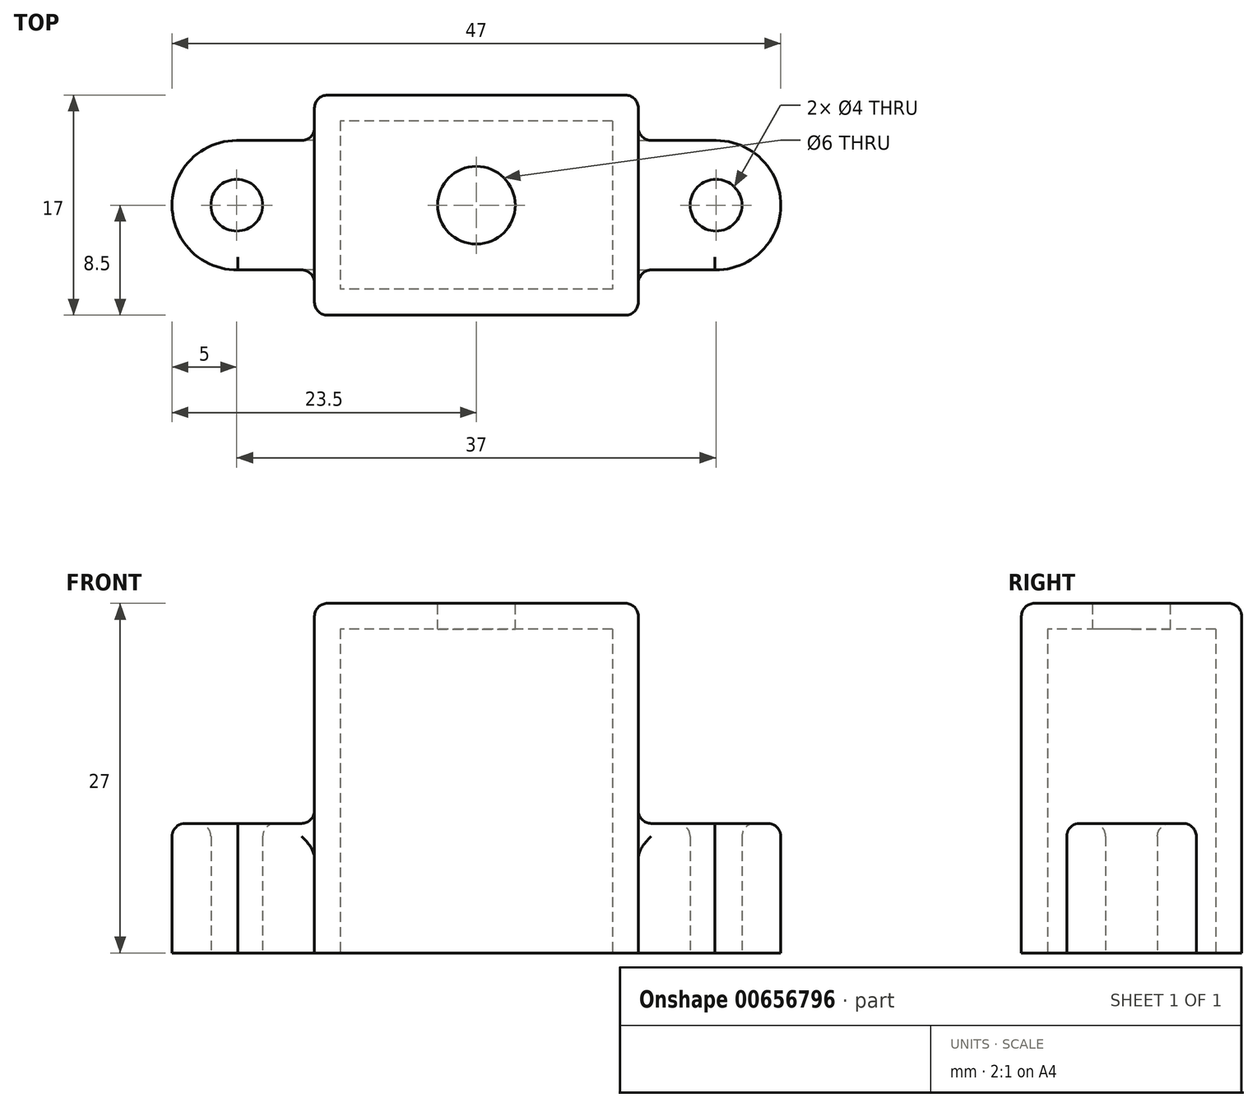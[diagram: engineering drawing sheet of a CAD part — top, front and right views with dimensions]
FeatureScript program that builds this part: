
annotation { "Feature Type Name" : "Feature", "Feature Type Description" : "" }
export const myFeature = defineFeature(function(context is Context, id is Id, definition is map)
    precondition{}
    {
        {
            var Q0;
            Q0=qCreatedBy(makeId("Top.planeOp"),FACE);
            var sketch = newSketch(context, id + "F0", { "sketchPlane" : qUnion([Q0])});
            skPoint(sketch, "E0.middle", {"position": v(0, 0) * mm});
            skLineSegment(sketch, "E1.bottom", {"start": v(12.5, -8.5) * mm, "end": v(-12.5, -8.5) * mm});
            skLineSegment(sketch, "E1.top", {"start": v(12.5, 8.5) * mm, "end": v(-12.5, 8.5) * mm});
            skLineSegment(sketch, "E1.left", {"start": v(12.5, -8.5) * mm, "end": v(12.5, 8.5) * mm});
            skLineSegment(sketch, "E1.right", {"start": v(-12.5, -8.5) * mm, "end": v(-12.5, 8.5) * mm});
            skSolve(sketch);
        }
        {
            var Q0;
            Q0 = qSketchRegion(id + "F0", true);
            extrude(context, id + "F1", {"entities" : qUnion([Q0]), "depth" : 27 * mm, "offsetDistance" : 25 * mm});
        }
        {
            var Q0;
            Q0=makeQuery(id+"F1.opExtrude","CAP_FACE",FACE,{"disambiguationData":[OSD([sQuery(id+"F0.wireOp",EDGE,"E1.bottom"),sQuery(id+"F0.wireOp",EDGE,"E1.top"),sQuery(id+"F0.wireOp",EDGE,"E1.left"),sQuery(id+"F0.wireOp",EDGE,"E1.right")])],"isStart":true});
            var sketch = newSketch(context, id + "F2", { "sketchPlane" : qUnion([Q0])});
            skLineSegment(sketch, "E2.bottom", {"start": v(10.5, -6.5) * mm, "end": v(-10.5, -6.5) * mm});
            skLineSegment(sketch, "E2.top", {"start": v(10.5, 6.5) * mm, "end": v(-10.5, 6.5) * mm});
            skLineSegment(sketch, "E2.left", {"start": v(10.5, -6.5) * mm, "end": v(10.5, 6.5) * mm});
            skLineSegment(sketch, "E2.right", {"start": v(-10.5, -6.5) * mm, "end": v(-10.5, 6.5) * mm});
            skPoint(sketch, "E2.middle", {"position": v(0, 0) * mm});
            skSolve(sketch);
        }
        {
            var Q0;
            Q0 = qSketchRegion(id + "F2", true);
            extrude(context, id + "F3", {"entities" : qUnion([Q0]), "operationType" : NewBodyOperationType.REMOVE, "oppositeDirection" : true, "depth" : 25 * mm, "offsetDistance" : 25 * mm});
        }
        {
            var Q0;
            Q0=qCreatedBy(makeId("Top.planeOp"),FACE);
            var sketch = newSketch(context, id + "F4", { "sketchPlane" : qUnion([Q0])});
            skArc(sketch, "E3", {"start": v(18.41, -5) * mm, "mid": v(23.5, -0.04) * mm, "end": v(18.5, 5) * mm});
            skLineSegment(sketch, "E4", {"start": v(18.5, 5) * mm, "end": v(12.5, 5) * mm});
            skLineSegment(sketch, "E5", {"start": v(12.5, 5) * mm, "end": v(12.5, -5) * mm});
            skLineSegment(sketch, "E6", {"start": v(12.5, -5) * mm, "end": v(18.59, -5) * mm});
            skCircle(sketch, "E7", {"center": v(18.5, 0) * mm, "radius": 2 * mm});
            skArc(sketch, "E8.MirrorCS", {"start": v(-18.41, -5) * mm, "mid": v(-23.5, -0.04) * mm, "end": v(-18.5, 5) * mm});
            skLineSegment(sketch, "E9.MirrorCS", {"start": v(-18.5, 5) * mm, "end": v(-12.5, 5) * mm});
            skLineSegment(sketch, "E10.MirrorCS", {"start": v(-12.5, -5) * mm, "end": v(-18.59, -5) * mm});
            skLineSegment(sketch, "E11.MirrorCS", {"start": v(-12.5, 5) * mm, "end": v(-12.5, -5) * mm});
            skCircle(sketch, "E12.MirrorC", {"center": v(-18.5, 0) * mm, "radius": 2 * mm});
            skSolve(sketch);
        }
        {
            var Q0;
            Q0 = qSketchRegion(id + "F4", true);
            extrude(context, id + "F5", {"entities" : qUnion([Q0]), "operationType" : NewBodyOperationType.ADD, "depth" : 10 * mm, "offsetDistance" : 25 * mm});
        }
        {
            var Q0;
            Q0=makeQuery(id+"F1.opExtrude","CAP_FACE",FACE,{"disambiguationData":[OSD([sQuery(id+"F0.wireOp",EDGE,"E1.bottom"),sQuery(id+"F0.wireOp",EDGE,"E1.top"),sQuery(id+"F0.wireOp",EDGE,"E1.left"),sQuery(id+"F0.wireOp",EDGE,"E1.right")])],"isStart":false});
            var sketch = newSketch(context, id + "F6", { "sketchPlane" : qUnion([Q0])});
            skCircle(sketch, "E13", {"center": v(0, 0) * mm, "radius": 3 * mm});
            skSolve(sketch);
        }
        {
            var Q0;
            Q0 = qSketchRegion(id + "F6", true);
            extrude(context, id + "F7", {"entities" : qUnion([Q0]), "operationType" : NewBodyOperationType.REMOVE, "endBound" : BoundingType.THROUGH_ALL, "oppositeDirection" : true, "depth" : 25 * mm, "offsetDistance" : 25 * mm});
        }
        {
            var Q0;
            Q0=makeQuery(id+"F1.opExtrude","SWEPT_EDGE",EDGE,{"disambiguationData":[OSD([sQuery(id+"F0.wireOp",EDGE,"E1.top"),sQuery(id+"F0.wireOp",EDGE,"E1.left")])]});
            var Q1;
            Q1=makeQuery(id+"F1.opExtrude","SWEPT_EDGE",EDGE,{"disambiguationData":[OSD([sQuery(id+"F0.wireOp",EDGE,"E1.top"),sQuery(id+"F0.wireOp",EDGE,"E1.right")])]});
            var Q2;
            Q2=makeQuery(id+"F1.opExtrude","SWEPT_EDGE",EDGE,{"disambiguationData":[OSD([sQuery(id+"F0.wireOp",EDGE,"E1.bottom"),sQuery(id+"F0.wireOp",EDGE,"E1.left")])]});
            var Q3;
            Q3=makeQuery(id+"F1.opExtrude","SWEPT_EDGE",EDGE,{"disambiguationData":[OSD([sQuery(id+"F0.wireOp",EDGE,"E1.bottom"),sQuery(id+"F0.wireOp",EDGE,"E1.right")])]});
            var Q4;
            Q4=makeQuery(id+"F1.opExtrude","CAP_EDGE",EDGE,{"disambiguationData":[OSD([sQuery(id+"F0.wireOp",EDGE,"E1.right")])],"isStart":false});
            var Q5;
            Q5=makeQuery(id+"F1.opExtrude","CAP_EDGE",EDGE,{"disambiguationData":[OSD([sQuery(id+"F0.wireOp",EDGE,"E1.bottom")])],"isStart":false});
            var Q6;
            Q6=makeQuery(id+"F1.opExtrude","CAP_EDGE",EDGE,{"disambiguationData":[OSD([sQuery(id+"F0.wireOp",EDGE,"E1.left")])],"isStart":false});
            var Q7;
            Q7=makeQuery(id+"F1.opExtrude","CAP_EDGE",EDGE,{"disambiguationData":[OSD([sQuery(id+"F0.wireOp",EDGE,"E1.top")])],"isStart":false});
            var Q8;
            Q8=makeQuery(id+"F5.opExtrude","CAP_FACE",FACE,{"disambiguationData":[OSD([sQuery(id+"F4.wireOp",EDGE,"E3"),sQuery(id+"F4.wireOp",EDGE,"E4"),sQuery(id+"F4.wireOp",EDGE,"E5"),sQuery(id+"F4.wireOp",EDGE,"E6"),sQuery(id+"F4.wireOp",EDGE,"E7")])],"isStart":false});
            var Q9;
            Q9=makeQuery(id+"F5.opExtrude","CAP_FACE",FACE,{"disambiguationData":[OSD([sQuery(id+"F4.wireOp",EDGE,"E8.MirrorCS"),sQuery(id+"F4.wireOp",EDGE,"E9.MirrorCS"),sQuery(id+"F4.wireOp",EDGE,"E10.MirrorCS"),sQuery(id+"F4.wireOp",EDGE,"E11.MirrorCS"),sQuery(id+"F4.wireOp",EDGE,"E12.MirrorC")])],"isStart":false});
            fillet(context, id + "F8", {"entities" : qUnion([Q0, Q1, Q2, Q3, Q4, Q5, Q6, Q7, Q8, Q9]), "radius" : 1 * mm, "tangentPropagation" : true, "allowEdgeOverflow" : false});
        }
    });
